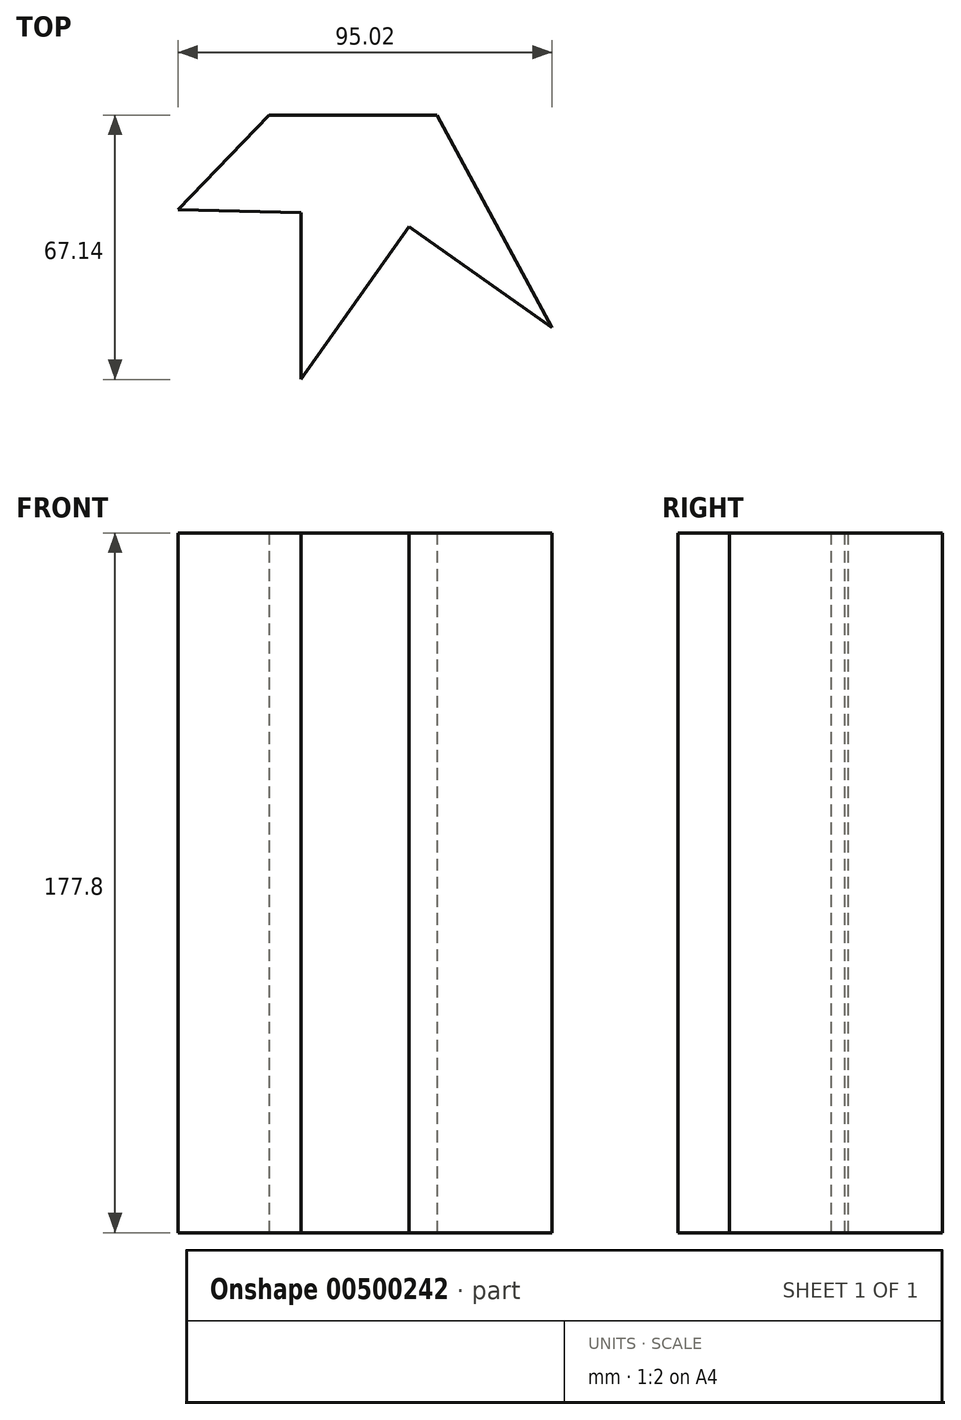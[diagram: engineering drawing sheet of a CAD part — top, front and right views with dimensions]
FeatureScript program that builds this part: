
annotation { "Feature Type Name" : "Feature", "Feature Type Description" : "" }
export const myFeature = defineFeature(function(context is Context, id is Id, definition is map)
    precondition{}
    {
        {
            var Q0;
            Q0=qCreatedBy(makeId("Top.planeOp"),FACE);
            var sketch = newSketch(context, id + "F0", { "sketchPlane" : qUnion([Q0])});
            skLineSegment(sketch, "E0", {"start": v(-58.67, 23.09) * mm, "end": v(-35.57, 47.06) * mm});
            skLineSegment(sketch, "E1", {"start": v(-35.57, 47.06) * mm, "end": v(7.15, 47.06) * mm});
            skLineSegment(sketch, "E2", {"start": v(7.15, 47.06) * mm, "end": v(36.35, -6.99) * mm});
            skLineSegment(sketch, "E3", {"start": v(36.35, -6.99) * mm, "end": v(0, 18.73) * mm});
            skLineSegment(sketch, "E4", {"start": v(0, 18.73) * mm, "end": v(-27.45, -20.08) * mm});
            skLineSegment(sketch, "E5", {"start": v(-27.45, -20.08) * mm, "end": v(-27.45, 22.22) * mm});
            skLineSegment(sketch, "E6", {"start": v(-27.45, 22.22) * mm, "end": v(-58.67, 23.09) * mm});
            skSolve(sketch);
        }
        {
            var Q0;
            Q0=makeQuery(id+"F0.imprint","IMPRINT",FACE,{"disambiguationData":[TD([[makeQuery(id+"F0.imprint","IMPRINT",EDGE,{"derivedFrom":sQuery(id+"F0.wireOp",EDGE,"E0")}),-1.0]])]});
            extrude(context, id + "F1", {"entities" : qUnion([Q0]), "depth" : 177.8 * mm});
        }
    });
